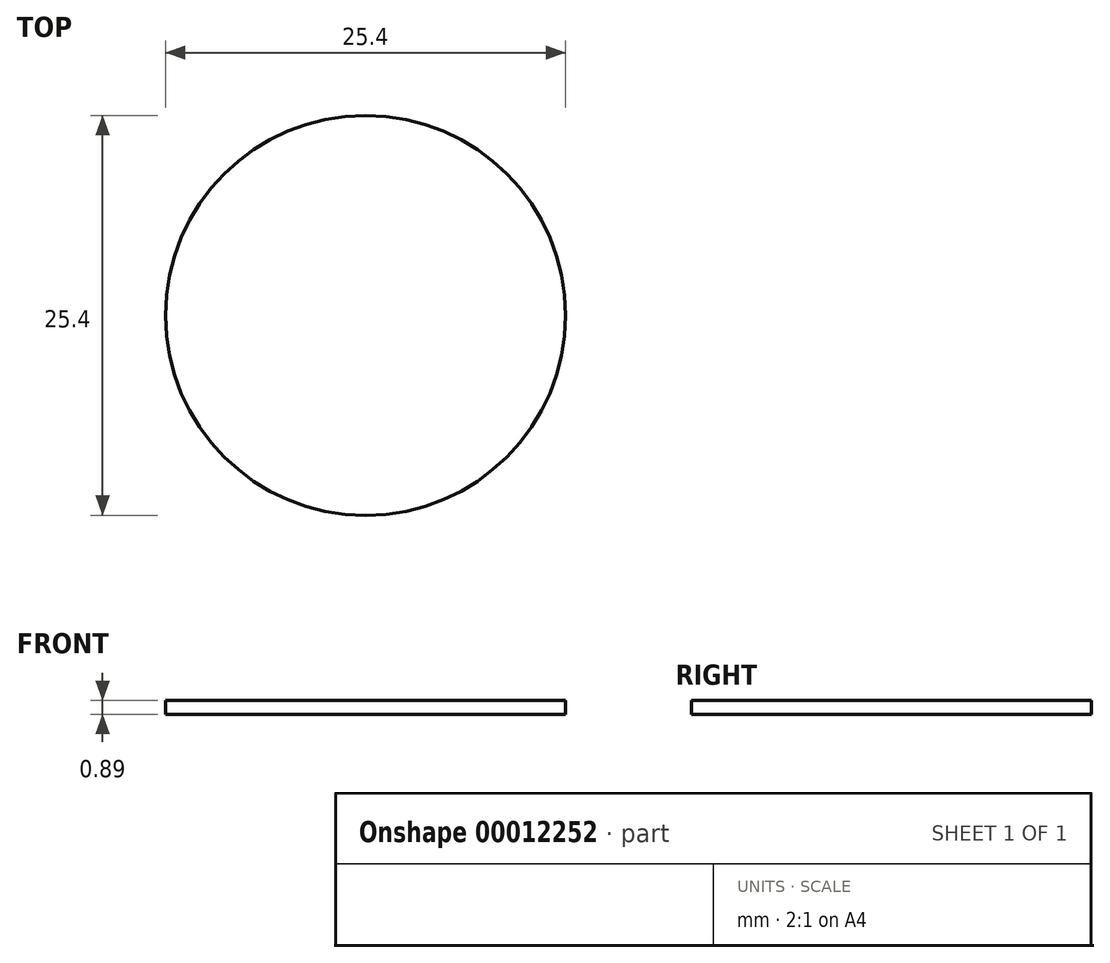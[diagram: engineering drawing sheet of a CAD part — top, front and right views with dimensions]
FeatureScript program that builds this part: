
annotation { "Feature Type Name" : "Feature", "Feature Type Description" : "" }
export const myFeature = defineFeature(function(context is Context, id is Id, definition is map)
    precondition{}
    {
        {
            var Q0;
            Q0=qCreatedBy(makeId("Top.planeOp"),FACE);
            var sketch = newSketch(context, id + "F0", { "sketchPlane" : qUnion([Q0])});
            skCircle(sketch, "E0", {"center": v(0, 0) * mm, "radius": 12.7 * mm});
            skSolve(sketch);
        }
        {
            var Q0;
            Q0 = qSketchRegion(id + "F0", true);
            extrude(context, id + "F1", {"entities" : qUnion([Q0]), "depth" : 0.89 * mm});
        }
    });
